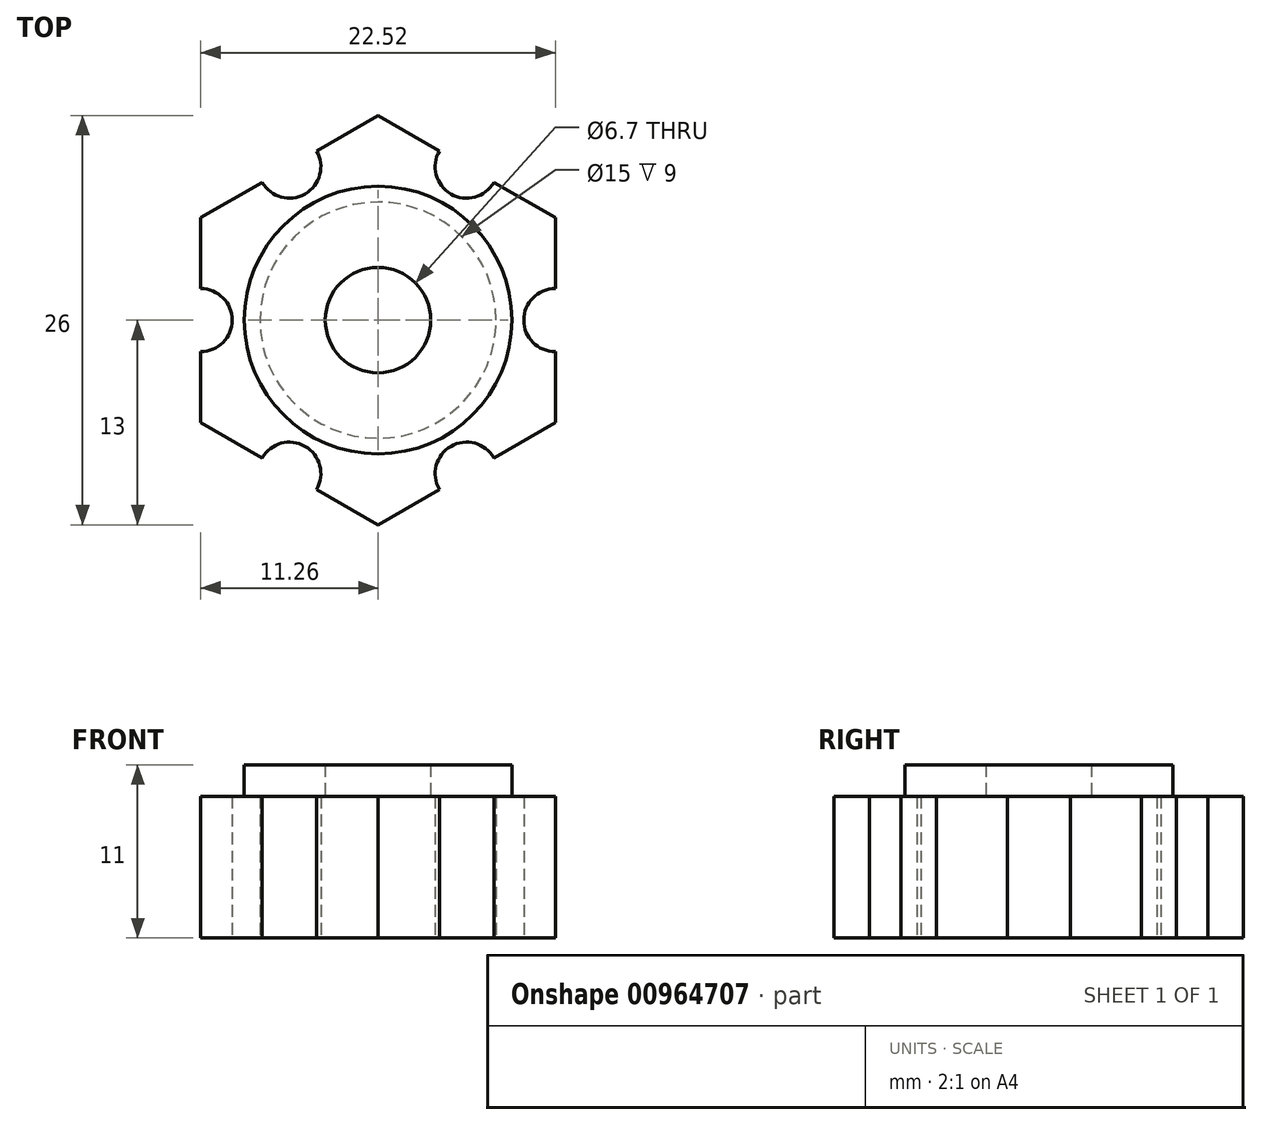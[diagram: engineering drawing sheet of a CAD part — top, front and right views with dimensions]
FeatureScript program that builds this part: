
annotation { "Feature Type Name" : "Feature", "Feature Type Description" : "" }
export const myFeature = defineFeature(function(context is Context, id is Id, definition is map)
    precondition{}
    {
        {
            var Q0;
            Q0=qCreatedBy(makeId("Top.planeOp"),FACE);
            var sketch = newSketch(context, id + "F0", { "sketchPlane" : qUnion([Q0])});
            skCircle(sketch, "E0.cCircle", {"center": v(0, 0) * mm, "radius": 11.26 * mm, "construction": true});
            skLineSegment(sketch, "E0.0", {"start": v(-11.26, -6.5) * mm, "end": v(-11.26, 6.5) * mm});
            skLineSegment(sketch, "E0.1", {"start": v(-11.26, 6.5) * mm, "end": v(0, 13) * mm});
            skLineSegment(sketch, "E0.2", {"start": v(0, 13) * mm, "end": v(11.26, 6.5) * mm});
            skLineSegment(sketch, "E0.3", {"start": v(11.26, 6.5) * mm, "end": v(11.26, -6.5) * mm});
            skLineSegment(sketch, "E0.4", {"start": v(11.26, -6.5) * mm, "end": v(0, -13) * mm});
            skLineSegment(sketch, "E0.5", {"start": v(0, -13) * mm, "end": v(-11.26, -6.5) * mm});
            skPoint(sketch, "E0.0.midPoint", {"position": v(-11.26, 0) * mm});
            skCircle(sketch, "E1", {"center": v(0, 0) * mm, "radius": 8.5 * mm});
            skCircle(sketch, "E2", {"center": v(0, 0) * mm, "radius": 3.35 * mm});
            skCircle(sketch, "E3", {"center": v(-5.63, 9.75) * mm, "radius": 2 * mm});
            skCircle(sketch, "E4", {"center": v(5.63, 9.75) * mm, "radius": 2 * mm});
            skCircle(sketch, "E5", {"center": v(11.26, 0) * mm, "radius": 2 * mm});
            skCircle(sketch, "E6", {"center": v(-5.63, -9.75) * mm, "radius": 2 * mm});
            skCircle(sketch, "E7", {"center": v(-11.26, 0) * mm, "radius": 2 * mm});
            skCircle(sketch, "E8", {"center": v(5.63, -9.75) * mm, "radius": 2 * mm});
            skSolve(sketch);
        }
        {
            var Q0;
            Q0=makeQuery(id+"F0.imprint","IMPRINT",FACE,{"disambiguationData":[TD([[makeQuery(id+"F0.imprint","IMPRINT",EDGE,{"derivedFrom":sQuery(id+"F0.wireOp",EDGE,"E1")}),-1.0]])]});
            extrude(context, id + "F1", {"entities" : qUnion([Q0]), "depth" : 9 * mm, "offsetDistance" : 25 * mm});
        }
        {
            var Q0;
            Q0=makeQuery(id+"F0.imprint","IMPRINT",FACE,{"disambiguationData":[TD([[makeQuery(id+"F0.imprint","IMPRINT",EDGE,{"derivedFrom":sQuery(id+"F0.wireOp",EDGE,"E1")}),1.0]])]});
            extrude(context, id + "F2", {"entities" : qUnion([Q0]), "operationType" : NewBodyOperationType.ADD, "depth" : 11 * mm, "offsetDistance" : 25 * mm});
        }
        {
            var Q0;
            {var subQ0=sQuery(id+"F0.wireOp",EDGE,"E1");Q0=makeQuery(id+"F2.boolean.opBoolean","MERGE",FACE,{"derivedFrom":[makeQuery(id+"F1.opExtrude","CAP_FACE",FACE,{"disambiguationData":[OSD([sQuery(id+"F0.wireOp",EDGE,"E0.0"),sQuery(id+"F0.wireOp",EDGE,"E0.1"),sQuery(id+"F0.wireOp",EDGE,"E0.2"),sQuery(id+"F0.wireOp",EDGE,"E0.3"),sQuery(id+"F0.wireOp",EDGE,"E0.4"),sQuery(id+"F0.wireOp",EDGE,"E0.5"),subQ0,sQuery(id+"F0.wireOp",EDGE,"E3"),sQuery(id+"F0.wireOp",EDGE,"E4"),sQuery(id+"F0.wireOp",EDGE,"E5"),sQuery(id+"F0.wireOp",EDGE,"E6"),sQuery(id+"F0.wireOp",EDGE,"E7"),sQuery(id+"F0.wireOp",EDGE,"E8")])],"isStart":true}),makeQuery(id+"F2.opExtrude","CAP_FACE",FACE,{"disambiguationData":[OSD([subQ0,sQuery(id+"F0.wireOp",EDGE,"E2")])],"isStart":true})]});}
            var sketch = newSketch(context, id + "F3", { "sketchPlane" : qUnion([Q0])});
            skCircle(sketch, "E9", {"center": v(0, 0) * mm, "radius": 7.5 * mm});
            skCircle(sketch, "E10", {"center": v(0, 0) * mm, "radius": 2 * mm});
            skSolve(sketch);
        }
        {
            var Q0;
            Q0=makeQuery(id+"F3.imprint","IMPRINT",FACE,{"disambiguationData":[TD([[makeQuery(id+"F3.imprint","IMPRINT",EDGE,{"derivedFrom":sQuery(id+"F3.wireOp",EDGE,"E9")}),1.0]])]});
            extrude(context, id + "F4", {"entities" : qUnion([Q0]), "operationType" : NewBodyOperationType.REMOVE, "oppositeDirection" : true, "depth" : 9 * mm, "offsetDistance" : 25 * mm});
        }
    });
